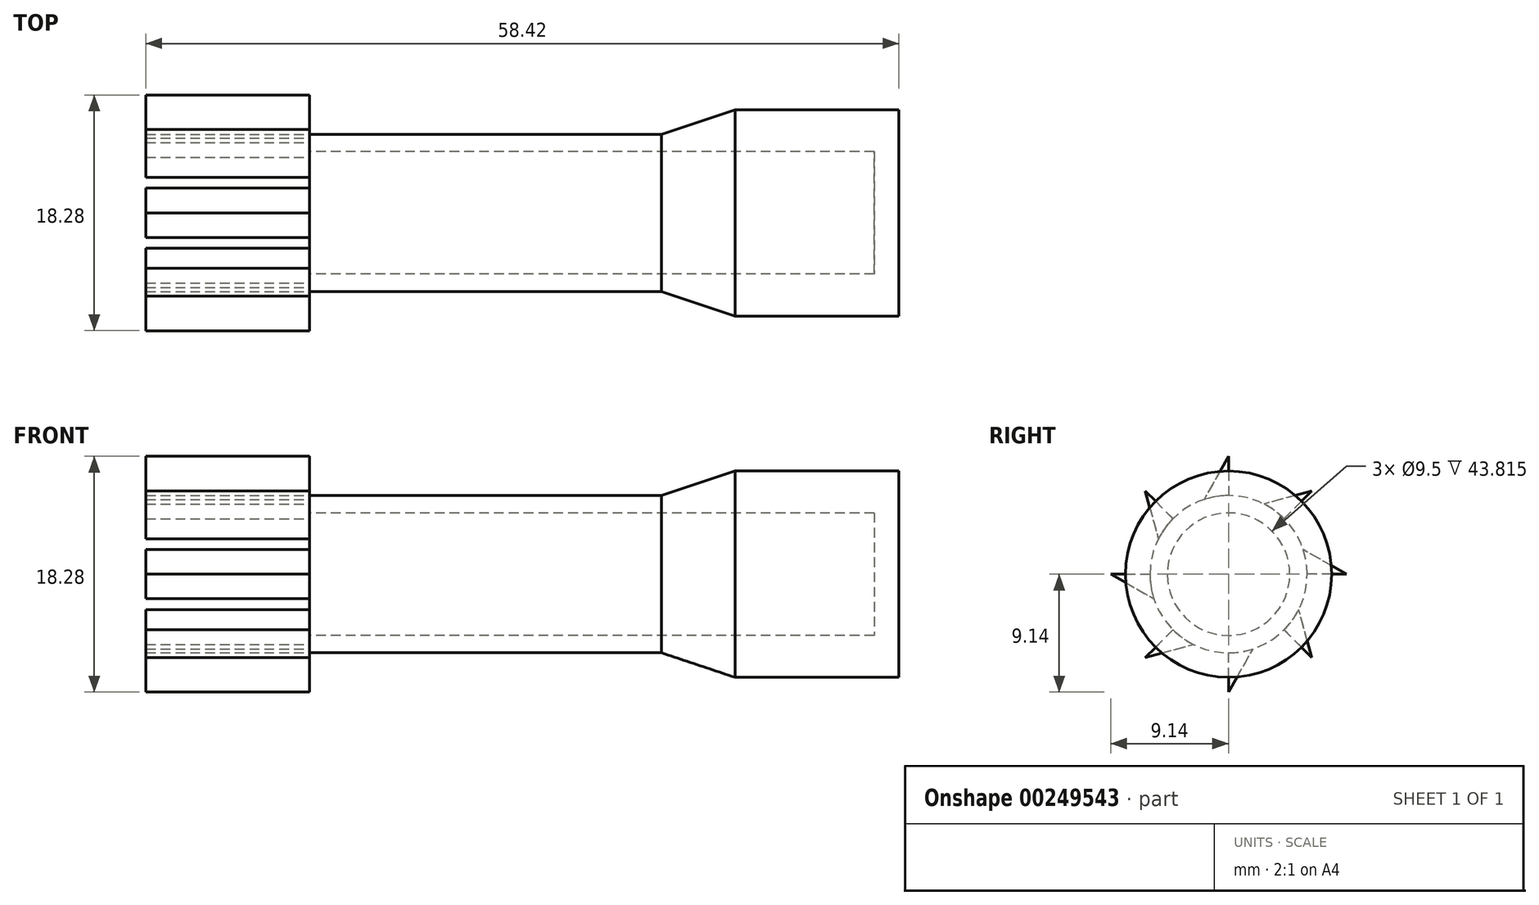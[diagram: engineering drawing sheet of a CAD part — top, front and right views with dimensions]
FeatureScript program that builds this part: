
annotation { "Feature Type Name" : "Feature", "Feature Type Description" : "" }
export const myFeature = defineFeature(function(context is Context, id is Id, definition is map)
    precondition{}
    {
        {
            var Q0;
            Q0=qCreatedBy(makeId("Front.planeOp"),FACE);
            var sketch = newSketch(context, id + "F0", { "sketchPlane" : qUnion([Q0])});
            skLineSegment(sketch, "E0.bottom", {"start": v(0, 0) * mm, "end": v(-45.72, 0) * mm});
            skLineSegment(sketch, "E0.top", {"start": v(0, 6.1) * mm, "end": v(-45.72, 6.1) * mm});
            skLineSegment(sketch, "E0.left", {"start": v(0, 0) * mm, "end": v(0, 6.1) * mm});
            skLineSegment(sketch, "E0.right", {"start": v(-45.72, 0) * mm, "end": v(-45.72, 6.1) * mm});
            skPoint(sketch, "E1.endSnap0", {"position": v(-45.72, 3.05) * mm});
            skLineSegment(sketch, "E2", {"start": v(-33.02, 6.1) * mm, "end": v(-45.72, 6.1) * mm});
            skLineSegment(sketch, "E3", {"start": v(0, 0) * mm, "end": v(0, 8) * mm});
            skPoint(sketch, "E3.endSnap0", {"position": v(0, 3.05) * mm});
            skLineSegment(sketch, "E4", {"start": v(0, 8) * mm, "end": v(-12.7, 8) * mm});
            skLineSegment(sketch, "E5", {"start": v(-18.41, 6.1) * mm, "end": v(0, 6.1) * mm});
            skLineSegment(sketch, "E6", {"start": v(-12.7, 8) * mm, "end": v(-18.41, 6.1) * mm});
            skLineSegment(sketch, "E7", {"start": v(-2.95, 8) * mm, "end": v(0, 8) * mm});
            skLineSegment(sketch, "E8", {"start": v(-2.95, 8) * mm, "end": v(-2.95, 9.14) * mm});
            skLineSegment(sketch, "E9", {"start": v(-2.95, 9.14) * mm, "end": v(0, 8) * mm});
            skLineSegment(sketch, "E10", {"start": v(-45.72, 6.1) * mm, "end": v(-45.72, 9.14) * mm});
            skLineSegment(sketch, "E11", {"start": v(-33.02, 6.1) * mm, "end": v(-45.72, 9.14) * mm});
            skSolve(sketch);
        }
        {
            var Q0;
            {var subQ2=sQuery(id+"F0.wireOp",EDGE,"E2");Q0=makeQuery(id+"F0.imprint","IMPRINT",FACE,{"disambiguationData":[TD([[makeQuery(id+"F0.imprint","IMPRINT",EDGE,{"derivedFrom":subQ2}),-1.0]])]});}
            var Q1;
            {var subQ2=sQuery(id+"F0.wireOp",EDGE,"E0.bottom");Q1=makeQuery(id+"F0.imprint","IMPRINT",FACE,{"disambiguationData":[TD([[makeQuery(id+"F0.imprint","IMPRINT",EDGE,{"derivedFrom":subQ2}),-1.0]])]});}
            var Q2;
            Q2=makeQuery(id+"F0.imprint","IMPRINT",FACE,{"disambiguationData":[TD([[makeQuery(id+"F0.imprint","IMPRINT",EDGE,{"derivedFrom":sQuery(id+"F0.wireOp",EDGE,"E4")}),1.0]])]});
            var Q3;
            Q3=makeQuery(id+"F0.imprint","IMPRINT",FACE,{"disambiguationData":[TD([[makeQuery(id+"F0.imprint","IMPRINT",EDGE,{"derivedFrom":sQuery(id+"F0.wireOp",EDGE,"E7")}),1.0]])]});
            var Q4;
            Q4=sQuery(id+"F0.wireOp",EDGE,"E0.bottom");
            revolve(context, id + "F1", {"entities" : qUnion([Q0, Q1, Q2, Q3]), "axis" : qUnion([Q4]), "revolveType" : RevolveType.FULL});
        }
        {
            var Q0;
            Q0=makeQuery(id+"F1.opRevolve","SWEPT_FACE",FACE,{"disambiguationData":[OSD([sQuery(id+"F0.wireOp",EDGE,"E0.right"),sQuery(id+"F0.wireOp",EDGE,"E10")])]});
            var sketch = newSketch(context, id + "F2", { "sketchPlane" : qUnion([Q0])});
            skCircle(sketch, "E12", {"center": v(0, 0) * mm, "radius": 4.75 * mm});
            skSolve(sketch);
        }
        {
            var Q0;
            Q0=makeQuery(id+"F2.imprint","IMPRINT",FACE,{"disambiguationData":[TD([[makeQuery(id+"F2.imprint","IMPRINT",EDGE,{"derivedFrom":sQuery(id+"F2.wireOp",EDGE,"E12")}),1.0]])]});
            extrude(context, id + "F3", {"entities" : qUnion([Q0]), "operationType" : NewBodyOperationType.REMOVE, "oppositeDirection" : true, "depth" : 43.81 * mm});
        }
        {
            var Q0;
            Q0=makeQuery(id+"F1.opRevolve","SWEPT_FACE",FACE,{"disambiguationData":[OSD([sQuery(id+"F0.wireOp",EDGE,"E0.right"),sQuery(id+"F0.wireOp",EDGE,"E10")])]});
            var sketch = newSketch(context, id + "F4", { "sketchPlane" : qUnion([Q0])});
            skCircle(sketch, "E13", {"center": v(0, 0) * mm, "radius": 6.1 * mm});
            skSolve(sketch);
        }
        {
            var Q0;
            Q0=makeQuery(id+"F1.opRevolve","SWEPT_BODY",BODY,{"disambiguationData":[OSD([sQuery(id+"F0.wireOp",EDGE,"E0.bottom"),sQuery(id+"F0.wireOp",EDGE,"E0.top"),sQuery(id+"F0.wireOp",EDGE,"E0.right"),sQuery(id+"F0.wireOp",EDGE,"E3"),sQuery(id+"F0.wireOp",EDGE,"E4"),sQuery(id+"F0.wireOp",EDGE,"E6"),sQuery(id+"F0.wireOp",EDGE,"E8"),sQuery(id+"F0.wireOp",EDGE,"E9"),sQuery(id+"F0.wireOp",EDGE,"E10"),sQuery(id+"F0.wireOp",EDGE,"E11")])]});
            transform(context, id + "F5", {"entities" : qUnion([Q0]), "transformType" : TransformType.TRANSLATION_3D, "dx" : 0 * mm, "dy" : 0 * mm, "dz" : 0 * mm, "makeCopy" : true});
        }
        {
            var Q0;
            Q0=makeQuery(id+"F1.opRevolve","SWEPT_BODY",BODY,{"disambiguationData":[OSD([sQuery(id+"F0.wireOp",EDGE,"E0.bottom"),sQuery(id+"F0.wireOp",EDGE,"E0.top"),sQuery(id+"F0.wireOp",EDGE,"E0.right"),sQuery(id+"F0.wireOp",EDGE,"E3"),sQuery(id+"F0.wireOp",EDGE,"E4"),sQuery(id+"F0.wireOp",EDGE,"E6"),sQuery(id+"F0.wireOp",EDGE,"E8"),sQuery(id+"F0.wireOp",EDGE,"E9"),sQuery(id+"F0.wireOp",EDGE,"E10"),sQuery(id+"F0.wireOp",EDGE,"E11")])]});
            transform(context, id + "F6", {"entities" : qUnion([Q0]), "transformType" : TransformType.TRANSLATION_3D, "dx" : 0 * mm, "dy" : 0 * mm, "dz" : 0 * mm, "makeCopy" : true});
        }
        {
            var Q0;
            Q0=makeQuery(id+"F4.imprint","IMPRINT",FACE,{"disambiguationData":[TD([[makeQuery(id+"F4.imprint","IMPRINT",EDGE,{"derivedFrom":sQuery(id+"F4.wireOp",EDGE,"E13")}),-1.0]])]});
            var sketch = newSketch(context, id + "F7", { "sketchPlane" : qUnion([Q0])});
            skCircle(sketch, "E14.0", {"center": v(0, 0) * mm, "radius": 9.14 * mm});
            skLineSegment(sketch, "E15", {"start": v(0, 9.14) * mm, "end": v(0, 6.1) * mm});
            skLineSegment(sketch, "E16", {"start": v(0, 9.14) * mm, "end": v(1.9, 5.79) * mm});
            skArc(sketch, "E17", {"start": v(1.9, 5.79) * mm, "mid": v(0.97, 6.02) * mm, "end": v(0, 6.1) * mm});
            skLineSegment(sketch, "E18.1.0", {"start": v(-6.47, 6.47) * mm, "end": v(-4.31, 4.31) * mm});
            skArc(sketch, "E18.1.1", {"start": v(-2.74, 5.44) * mm, "mid": v(-3.57, 4.94) * mm, "end": v(-4.31, 4.31) * mm});
            skLineSegment(sketch, "E18.1.2", {"start": v(-6.47, 6.47) * mm, "end": v(-2.74, 5.44) * mm});
            skLineSegment(sketch, "E18.2.0", {"start": v(-9.14, 0) * mm, "end": v(-6.1, 0) * mm});
            skArc(sketch, "E18.2.1", {"start": v(-5.79, 1.9) * mm, "mid": v(-6.02, 0.97) * mm, "end": v(-6.1, 0) * mm});
            skLineSegment(sketch, "E18.2.2", {"start": v(-9.14, 0) * mm, "end": v(-5.79, 1.9) * mm});
            skLineSegment(sketch, "E18.3.0", {"start": v(-6.47, -6.47) * mm, "end": v(-4.31, -4.31) * mm});
            skArc(sketch, "E18.3.1", {"start": v(-5.44, -2.74) * mm, "mid": v(-4.94, -3.57) * mm, "end": v(-4.31, -4.31) * mm});
            skLineSegment(sketch, "E18.3.2", {"start": v(-6.47, -6.47) * mm, "end": v(-5.44, -2.74) * mm});
            skLineSegment(sketch, "E18.4.0", {"start": v(0, -9.14) * mm, "end": v(0, -6.1) * mm});
            skArc(sketch, "E18.4.1", {"start": v(-1.9, -5.79) * mm, "mid": v(-0.97, -6.02) * mm, "end": v(0, -6.1) * mm});
            skLineSegment(sketch, "E18.4.2", {"start": v(0, -9.14) * mm, "end": v(-1.9, -5.79) * mm});
            skLineSegment(sketch, "E18.5.0", {"start": v(6.47, -6.47) * mm, "end": v(4.31, -4.31) * mm});
            skArc(sketch, "E18.5.1", {"start": v(2.74, -5.44) * mm, "mid": v(3.57, -4.94) * mm, "end": v(4.31, -4.31) * mm});
            skLineSegment(sketch, "E18.5.2", {"start": v(6.47, -6.47) * mm, "end": v(2.74, -5.44) * mm});
            skLineSegment(sketch, "E18.6.0", {"start": v(9.14, 0) * mm, "end": v(6.1, 0) * mm});
            skArc(sketch, "E18.6.1", {"start": v(5.79, -1.9) * mm, "mid": v(6.02, -0.97) * mm, "end": v(6.1, 0) * mm});
            skLineSegment(sketch, "E18.6.2", {"start": v(9.14, 0) * mm, "end": v(5.79, -1.9) * mm});
            skLineSegment(sketch, "E18.7.0", {"start": v(6.47, 6.47) * mm, "end": v(4.31, 4.31) * mm});
            skArc(sketch, "E18.7.1", {"start": v(5.44, 2.74) * mm, "mid": v(4.94, 3.57) * mm, "end": v(4.31, 4.31) * mm});
            skLineSegment(sketch, "E18.7.2", {"start": v(6.47, 6.47) * mm, "end": v(5.44, 2.74) * mm});
            skSolve(sketch);
        }
        {
            var Q0;
            Q0=makeQuery(id+"F7.imprint","IMPRINT",FACE,{"disambiguationData":[TD([[makeQuery(id+"F7.imprint","IMPRINT",EDGE,{"derivedFrom":sQuery(id+"F7.wireOp",EDGE,"E15")}),1.0]])]});
            var Q1;
            Q1=makeQuery(id+"F7.imprint","IMPRINT",FACE,{"disambiguationData":[TD([[makeQuery(id+"F7.imprint","IMPRINT",EDGE,{"derivedFrom":sQuery(id+"F7.wireOp",EDGE,"E18.7.0")}),1.0]])]});
            var Q2;
            Q2=makeQuery(id+"F7.imprint","IMPRINT",FACE,{"disambiguationData":[TD([[makeQuery(id+"F7.imprint","IMPRINT",EDGE,{"derivedFrom":sQuery(id+"F7.wireOp",EDGE,"E18.6.0")}),1.0]])]});
            var Q3;
            Q3=makeQuery(id+"F7.imprint","IMPRINT",FACE,{"disambiguationData":[TD([[makeQuery(id+"F7.imprint","IMPRINT",EDGE,{"derivedFrom":sQuery(id+"F7.wireOp",EDGE,"E18.5.0")}),1.0]])]});
            var Q4;
            Q4=makeQuery(id+"F7.imprint","IMPRINT",FACE,{"disambiguationData":[TD([[makeQuery(id+"F7.imprint","IMPRINT",EDGE,{"derivedFrom":sQuery(id+"F7.wireOp",EDGE,"E18.4.0")}),1.0]])]});
            var Q5;
            Q5=makeQuery(id+"F7.imprint","IMPRINT",FACE,{"disambiguationData":[TD([[makeQuery(id+"F7.imprint","IMPRINT",EDGE,{"derivedFrom":sQuery(id+"F7.wireOp",EDGE,"E18.3.0")}),1.0]])]});
            var Q6;
            Q6=makeQuery(id+"F7.imprint","IMPRINT",FACE,{"disambiguationData":[TD([[makeQuery(id+"F7.imprint","IMPRINT",EDGE,{"derivedFrom":sQuery(id+"F7.wireOp",EDGE,"E18.2.0")}),1.0]])]});
            var Q7;
            Q7=makeQuery(id+"F7.imprint","IMPRINT",FACE,{"disambiguationData":[TD([[makeQuery(id+"F7.imprint","IMPRINT",EDGE,{"derivedFrom":sQuery(id+"F7.wireOp",EDGE,"E18.1.0")}),1.0]])]});
            extrude(context, id + "F8", {"entities" : qUnion([Q0, Q1, Q2, Q3, Q4, Q5, Q6, Q7]), "depth" : 12.7 * mm});
        }
    });
